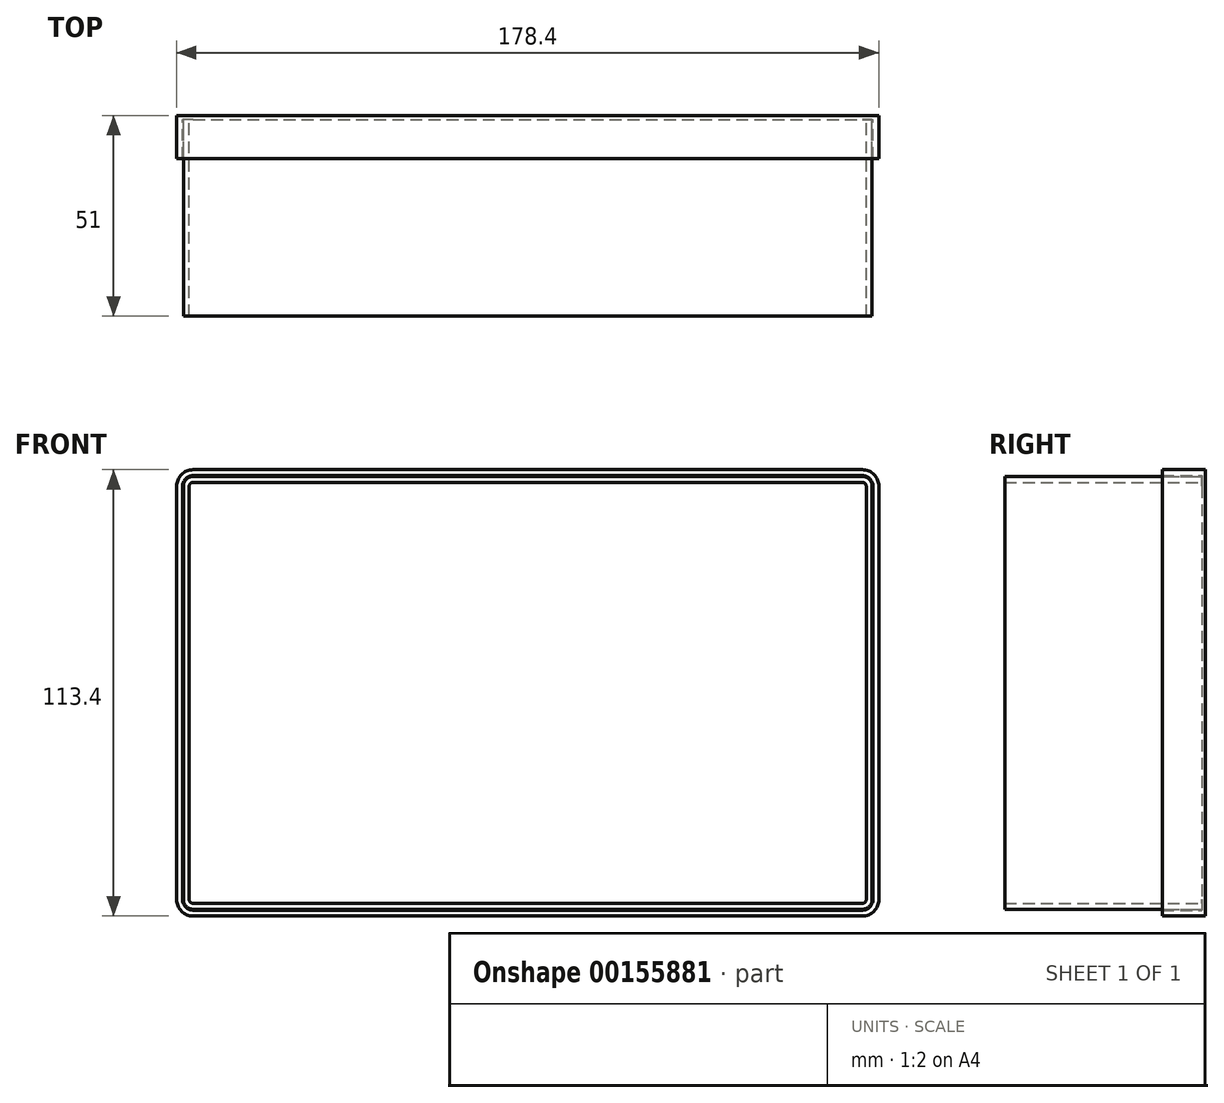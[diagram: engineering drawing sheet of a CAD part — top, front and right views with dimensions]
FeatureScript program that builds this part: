
annotation { "Feature Type Name" : "Feature", "Feature Type Description" : "" }
export const myFeature = defineFeature(function(context is Context, id is Id, definition is map)
    precondition{}
    {
        {
            assignVariable(context, id + "F0", {"name" : "Tjocklek", "anyValue" : 1.5});
        }
        {
            assignVariable(context, id + "F1", {"name" : "Djup", "anyValue" : 50});
        }
        {
            var Q0;
            Q0=qCreatedBy(makeId("Front.planeOp"),FACE);
            var sketch = newSketch(context, id + "F2", { "sketchPlane" : qUnion([Q0])});
            skLineSegment(sketch, "E0.bottom", {"start": v(-85, 53.5) * mm, "end": v(85, 53.5) * mm});
            skLineSegment(sketch, "E0.top", {"start": v(-85, -53.5) * mm, "end": v(85, -53.5) * mm});
            skLineSegment(sketch, "E0.left", {"start": v(-86, 52.5) * mm, "end": v(-86, -52.5) * mm});
            skLineSegment(sketch, "E0.right", {"start": v(86, 52.5) * mm, "end": v(86, -52.5) * mm});
            skLineSegment(sketch, "E1.0", {"start": v(87.5, 52.5) * mm, "end": v(87.5, -52.5) * mm});
            skLineSegment(sketch, "E1.1", {"start": v(-85, 55) * mm, "end": v(85, 55) * mm});
            skLineSegment(sketch, "E1.2", {"start": v(-87.5, 52.5) * mm, "end": v(-87.5, -52.5) * mm});
            skLineSegment(sketch, "E1.3", {"start": v(-85, -55) * mm, "end": v(85, -55) * mm});
            skPoint(sketch, "E2.visualSharp", {"position": v(-87.5, 55) * mm});
            skArc(sketch, "E2.filletArc", {"start": v(-85, 55) * mm, "mid": v(-86.77, 54.27) * mm, "end": v(-87.5, 52.5) * mm});
            skPoint(sketch, "E3.visualSharp", {"position": v(87.5, 55) * mm});
            skArc(sketch, "E3.filletArc", {"start": v(87.5, 52.5) * mm, "mid": v(86.77, 54.27) * mm, "end": v(85, 55) * mm});
            skPoint(sketch, "E4.visualSharp", {"position": v(87.5, -55) * mm});
            skArc(sketch, "E4.filletArc", {"start": v(85, -55) * mm, "mid": v(86.77, -54.27) * mm, "end": v(87.5, -52.5) * mm});
            skPoint(sketch, "E5.visualSharp", {"position": v(-87.5, -55) * mm});
            skArc(sketch, "E5.filletArc", {"start": v(-87.5, -52.5) * mm, "mid": v(-86.77, -54.27) * mm, "end": v(-85, -55) * mm});
            skPoint(sketch, "E6.visualSharp", {"position": v(-86, -53.5) * mm});
            skArc(sketch, "E6.filletArc", {"start": v(-86, -52.5) * mm, "mid": v(-85.7, -53.2) * mm, "end": v(-85, -53.5) * mm});
            skPoint(sketch, "E7.visualSharp", {"position": v(86, -53.5) * mm});
            skPoint(sketch, "E8.visualSharp", {"position": v(86, 53.5) * mm});
            skArc(sketch, "E8.filletArc", {"start": v(86, 52.5) * mm, "mid": v(85.7, 53.2) * mm, "end": v(85, 53.5) * mm});
            skPoint(sketch, "E9.visualSharp", {"position": v(-86, 53.5) * mm});
            skArc(sketch, "E9.filletArc", {"start": v(-85, 53.5) * mm, "mid": v(-85.7, 53.2) * mm, "end": v(-86, 52.5) * mm});
            skArc(sketch, "E10.filletArc", {"start": v(85, -53.5) * mm, "mid": v(85.7, -53.2) * mm, "end": v(86, -52.5) * mm});
            skLineSegment(sketch, "E11", {"start": v(-86, 0) * mm, "end": v(86, 0) * mm, "construction": true});
            skSolve(sketch);
        }
        {
            var Q0;
            Q0=makeQuery(id+"F2.imprint","IMPRINT",FACE,{"disambiguationData":[TD([[makeQuery(id+"F2.imprint","IMPRINT",EDGE,{"derivedFrom":sQuery(id+"F2.wireOp",EDGE,"E0.bottom")}),1.0]])]});
            extrude(context, id + "F3", {"entities" : qUnion([Q0]), "depth" : (getVariable(context, 'Djup')) * mm});
        }
        {
            var Q0;
            Q0=qCreatedBy(makeId("Front.planeOp"),FACE);
            var sketch = newSketch(context, id + "F4", { "sketchPlane" : qUnion([Q0])});
            skLineSegment(sketch, "E12.0", {"start": v(-85, -55.2) * mm, "end": v(85, -55.2) * mm});
            skLineSegment(sketch, "E12.1", {"start": v(-87.7, 52.5) * mm, "end": v(-87.7, -52.5) * mm});
            skLineSegment(sketch, "E12.2", {"start": v(-85, 55.2) * mm, "end": v(85, 55.2) * mm});
            skLineSegment(sketch, "E12.3", {"start": v(87.7, 52.5) * mm, "end": v(87.7, -52.5) * mm});
            skLineSegment(sketch, "E13.0", {"start": v(-85, -56.7) * mm, "end": v(85, -56.7) * mm});
            skLineSegment(sketch, "E13.1", {"start": v(-89.2, 52.5) * mm, "end": v(-89.2, -52.5) * mm});
            skLineSegment(sketch, "E13.2", {"start": v(-85, 56.7) * mm, "end": v(85, 56.7) * mm});
            skLineSegment(sketch, "E13.3", {"start": v(89.2, 52.5) * mm, "end": v(89.2, -52.5) * mm});
            skPoint(sketch, "E14.visualSharp", {"position": v(-87.7, 55.2) * mm});
            skArc(sketch, "E14.filletArc", {"start": v(-85, 55.2) * mm, "mid": v(-86.9, 54.4) * mm, "end": v(-87.7, 52.5) * mm});
            skPoint(sketch, "E15.visualSharp", {"position": v(87.7, 55.2) * mm});
            skArc(sketch, "E15.filletArc", {"start": v(87.7, 52.5) * mm, "mid": v(86.9, 54.4) * mm, "end": v(85, 55.2) * mm});
            skPoint(sketch, "E16.visualSharp", {"position": v(87.7, -55.2) * mm});
            skArc(sketch, "E16.filletArc", {"start": v(85, -55.2) * mm, "mid": v(86.9, -54.4) * mm, "end": v(87.7, -52.5) * mm});
            skPoint(sketch, "E17.visualSharp", {"position": v(-87.7, -55.2) * mm});
            skArc(sketch, "E17.filletArc", {"start": v(-87.7, -52.5) * mm, "mid": v(-86.9, -54.4) * mm, "end": v(-85, -55.2) * mm});
            skPoint(sketch, "E18.visualSharp", {"position": v(-89.2, 56.7) * mm});
            skArc(sketch, "E18.filletArc", {"start": v(-85, 56.7) * mm, "mid": v(-87.97, 55.47) * mm, "end": v(-89.2, 52.5) * mm});
            skPoint(sketch, "E19.visualSharp", {"position": v(89.2, 56.7) * mm});
            skArc(sketch, "E19.filletArc", {"start": v(89.2, 52.5) * mm, "mid": v(87.97, 55.47) * mm, "end": v(85, 56.7) * mm});
            skPoint(sketch, "E20.visualSharp", {"position": v(89.2, -56.7) * mm});
            skArc(sketch, "E20.filletArc", {"start": v(85, -56.7) * mm, "mid": v(87.97, -55.47) * mm, "end": v(89.2, -52.5) * mm});
            skPoint(sketch, "E21.visualSharp", {"position": v(-89.2, -56.7) * mm});
            skArc(sketch, "E21.filletArc", {"start": v(-89.2, -52.5) * mm, "mid": v(-87.97, -55.47) * mm, "end": v(-85, -56.7) * mm});
            skSolve(sketch);
        }
        {
            var Q0;
            Q0 = qSketchRegion(id + "F4", true);
            extrude(context, id + "F5", {"entities" : qUnion([Q0]), "depth" : 10 * mm});
        }
        {
            var Q0;
            Q0=makeQuery(id+"F5.opExtrude","CAP_FACE",FACE,{"disambiguationData":[OSD([sQuery(id+"F4.wireOp",EDGE,"E12.0"),sQuery(id+"F4.wireOp",EDGE,"E12.1"),sQuery(id+"F4.wireOp",EDGE,"E12.2"),sQuery(id+"F4.wireOp",EDGE,"E12.3"),sQuery(id+"F4.wireOp",EDGE,"E13.0"),sQuery(id+"F4.wireOp",EDGE,"E13.1"),sQuery(id+"F4.wireOp",EDGE,"E13.2"),sQuery(id+"F4.wireOp",EDGE,"E13.3"),sQuery(id+"F4.wireOp",EDGE,"E14.filletArc"),sQuery(id+"F4.wireOp",EDGE,"E15.filletArc"),sQuery(id+"F4.wireOp",EDGE,"E16.filletArc"),sQuery(id+"F4.wireOp",EDGE,"E17.filletArc"),sQuery(id+"F4.wireOp",EDGE,"E18.filletArc"),sQuery(id+"F4.wireOp",EDGE,"E19.filletArc"),sQuery(id+"F4.wireOp",EDGE,"E20.filletArc"),sQuery(id+"F4.wireOp",EDGE,"E21.filletArc")])],"isStart":true});
            var sketch = newSketch(context, id + "F6", { "sketchPlane" : qUnion([Q0])});
            skArc(sketch, "E22.0", {"start": v(-89.2, 52.5) * mm, "mid": v(-87.97, 55.47) * mm, "end": v(-85, 56.7) * mm});
            skLineSegment(sketch, "E23.0", {"start": v(85, 56.7) * mm, "end": v(-85, 56.7) * mm});
            skArc(sketch, "E24.0", {"start": v(85, 56.7) * mm, "mid": v(87.97, 55.47) * mm, "end": v(89.2, 52.5) * mm});
            skLineSegment(sketch, "E25.0", {"start": v(89.2, 52.5) * mm, "end": v(89.2, -52.5) * mm});
            skArc(sketch, "E26.0", {"start": v(89.2, -52.5) * mm, "mid": v(87.97, -55.47) * mm, "end": v(85, -56.7) * mm});
            skLineSegment(sketch, "E27.0", {"start": v(85, -56.7) * mm, "end": v(-85, -56.7) * mm});
            skArc(sketch, "E28.0", {"start": v(-85, -56.7) * mm, "mid": v(-87.97, -55.47) * mm, "end": v(-89.2, -52.5) * mm});
            skLineSegment(sketch, "E29.0", {"start": v(-89.2, 52.5) * mm, "end": v(-89.2, -52.5) * mm});
            skSolve(sketch);
        }
        {
            var Q0;
            Q0 = qSketchRegion(id + "F6", true);
            extrude(context, id + "F7", {"entities" : qUnion([Q0]), "operationType" : NewBodyOperationType.ADD, "depth" : (getVariable(context, 'Tjocklek') * 2 / 3) * mm});
        }
    });
